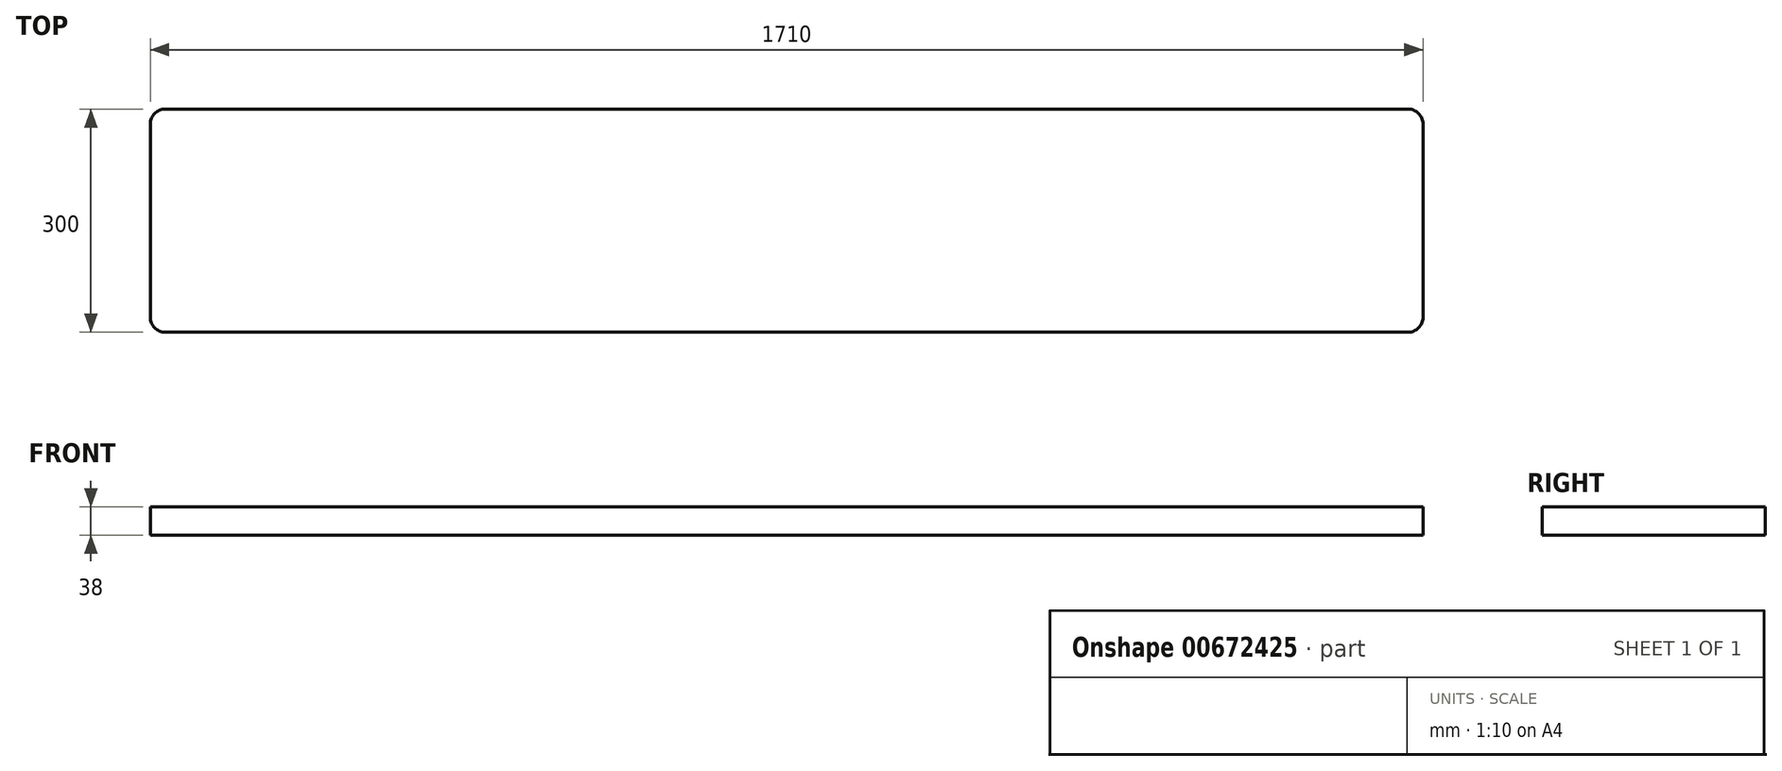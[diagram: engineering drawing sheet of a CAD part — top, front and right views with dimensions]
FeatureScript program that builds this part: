
annotation { "Feature Type Name" : "Feature", "Feature Type Description" : "" }
export const myFeature = defineFeature(function(context is Context, id is Id, definition is map)
    precondition{}
    {
        {
            var Q0;
            Q0=qCreatedBy(makeId("Top.planeOp"),FACE);
            var sketch = newSketch(context, id + "F0", { "sketchPlane" : qUnion([Q0])});
            skLineSegment(sketch, "E0.bottom", {"start": v(-830.65, 151.89) * mm, "end": v(879.35, 151.89) * mm});
            skLineSegment(sketch, "E0.top", {"start": v(-830.65, -148.11) * mm, "end": v(879.35, -148.11) * mm});
            skLineSegment(sketch, "E0.left", {"start": v(-830.65, 151.89) * mm, "end": v(-830.65, -148.11) * mm});
            skLineSegment(sketch, "E0.right", {"start": v(879.35, 151.89) * mm, "end": v(879.35, -148.11) * mm});
            skSolve(sketch);
        }
        {
            var Q0;
            Q0 = qSketchRegion(id + "F0", true);
            extrude(context, id + "F1", {"entities" : qUnion([Q0]), "depth" : 38 * mm, "offsetDistance" : 25 * mm});
        }
        {
            var Q0;
            Q0=makeQuery(id+"F1.opExtrude","SWEPT_EDGE",EDGE,{"disambiguationData":[OSD([sQuery(id+"F0.wireOp",EDGE,"E0.top"),sQuery(id+"F0.wireOp",EDGE,"E0.right")])]});
            var Q1;
            Q1=makeQuery(id+"F1.opExtrude","SWEPT_EDGE",EDGE,{"disambiguationData":[OSD([sQuery(id+"F0.wireOp",EDGE,"E0.bottom"),sQuery(id+"F0.wireOp",EDGE,"E0.right")])]});
            var Q2;
            Q2=makeQuery(id+"F1.opExtrude","SWEPT_EDGE",EDGE,{"disambiguationData":[OSD([sQuery(id+"F0.wireOp",EDGE,"E0.top"),sQuery(id+"F0.wireOp",EDGE,"E0.left")])]});
            var Q3;
            Q3=makeQuery(id+"F1.opExtrude","SWEPT_EDGE",EDGE,{"disambiguationData":[OSD([sQuery(id+"F0.wireOp",EDGE,"E0.bottom"),sQuery(id+"F0.wireOp",EDGE,"E0.left")])]});
            fillet(context, id + "F2", {"entities" : qUnion([Q0, Q1, Q2, Q3]), "radius" : 20 * mm, "tangentPropagation" : true, "allowEdgeOverflow" : false});
        }
    });
